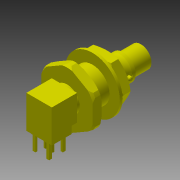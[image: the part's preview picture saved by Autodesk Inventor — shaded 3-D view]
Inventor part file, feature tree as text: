
AUTODESK INVENTOR PART (.ipt)
format: ipt  version: 2014 SP2 (Build 180246200, 246)  size: 385,024 bytes
history: native  units: mm
features: sketch x14, extrude x10, revolve x5
ambient origin geometry x8: Origin, YZ Plane, XZ Plane, XY Plane, X Axis, Y Axis, Z Axis, Center Point
bodies: Solid1 (feature_tree)
feature tree (29):
  extrude  "Extrusion1"  TaperAngle=360.0deg  [1 undecoded]
  revolve  "Revolution1"  Angle=360.0deg
  extrude  "Extrusion2"  Depth=0.15mm TaperAngle=0.0deg
  revolve  "Revolution2"  Angle=360.0deg
  revolve  "Revolution3"  [1 undecoded]
  extrude  "Extrusion3"  Depth=0.25mm TaperAngle=0.0deg
  extrude  "Extrusion4"  Depth=2.73575mm TaperAngle=0.0deg
  revolve  "Revolution4"  [1 undecoded]
  extrude  "Extrusion5"  [1 undecoded]
  extrude  "Extrusion6"  [1 undecoded]
  extrude  "Extrusion7"  [1 undecoded]
  sketch  "Sketch11"
  extrude  "Extrusion8"  [1 undecoded]
  extrude  "Extrusion9"  [1 undecoded]
  extrude  "Extrusion10"  [1 undecoded]
  revolve  "Revolution5"  [1 undecoded]
  sketch  "Sketch0"  dims[d0=4.7mm d1=0.0mm d2=360.0deg]
  sketch  "Sketch2"  dims[d6=360.0deg d7=0.15mm d8=0.0mm]
  sketch  "Sketch3"  dims[d9=0.15mm d10=0.0mm d11=360.0deg]
  sketch  "Sketch4"  dims[d12=1.65mm d13=0.0mm d14=2.0mm d15=0.0mm]
  sketch  "Sketch5"  dims[d16=0.25mm d17=0.0mm d18=2.7mm d19=0.0mm]
  sketch  "Sketch6"  dims[d20=2.73575mm d21=0.0mm d22=2.73575mm d23=0.0mm]
  sketch  "Sketch7"  dims[d24=360.0deg]
  sketch  "Sketch8"
  sketch  "Sketch9"
  sketch  "Sketch10"
  sketch  "Sketch12"
  sketch  "Sketch_1"  dims[d3=1.97mm d4=0.0mm d5=360.0deg]
  sketch  "Sketch13"
note: 10 required parameter values undecoded (feature->parameter linkage not recoverable at this tier; creation-order binding heuristic only, values carry confidence <= 0.55)